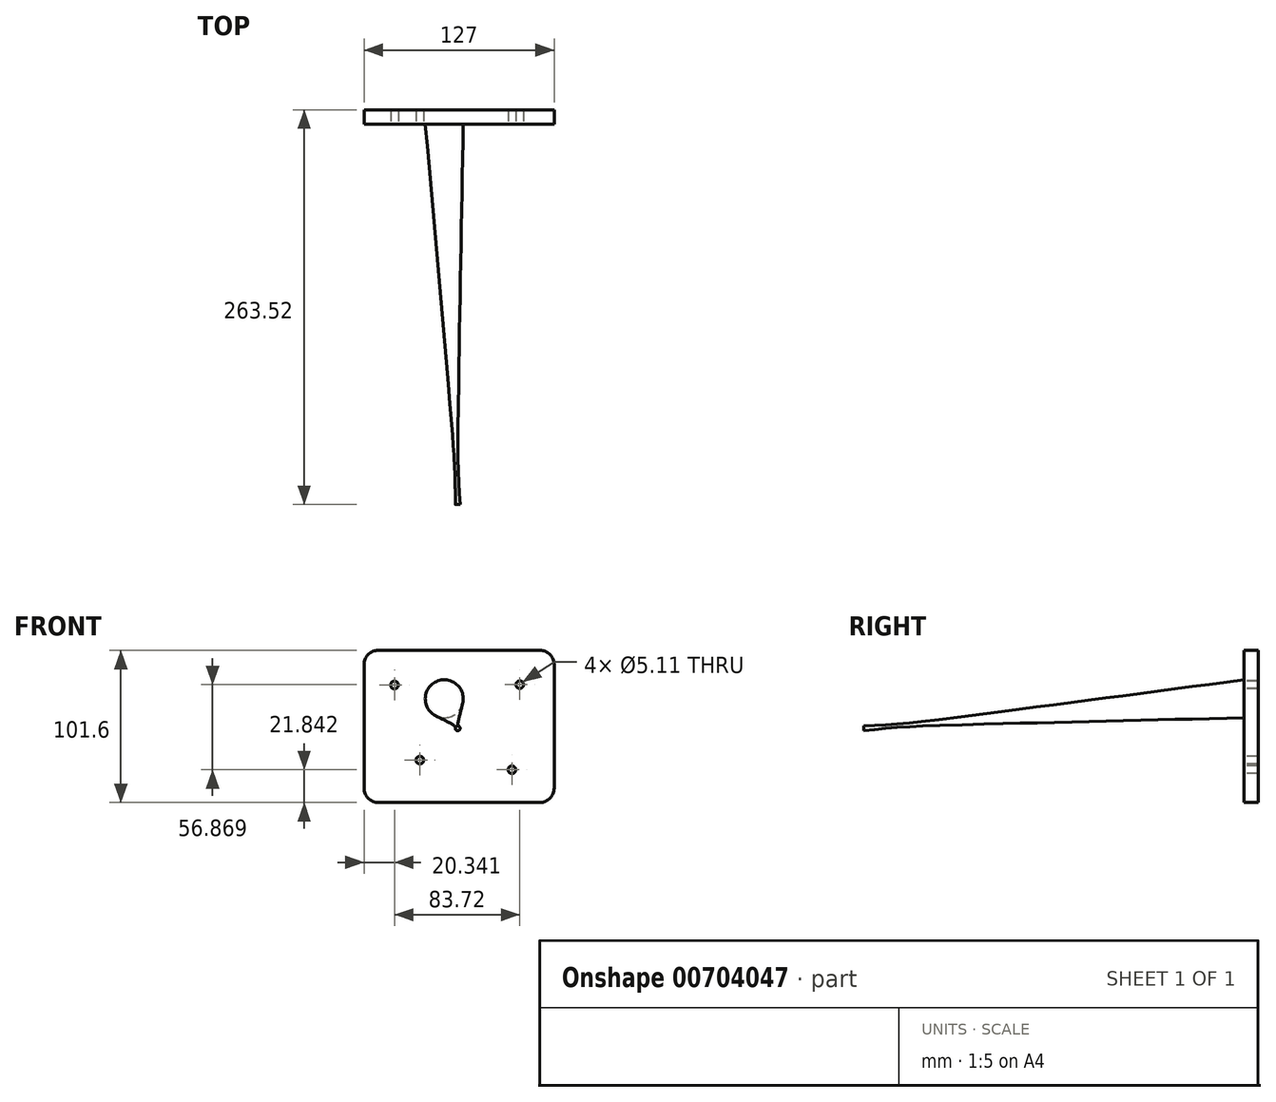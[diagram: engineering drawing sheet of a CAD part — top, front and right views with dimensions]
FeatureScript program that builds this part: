
annotation { "Feature Type Name" : "Feature", "Feature Type Description" : "" }
export const myFeature = defineFeature(function(context is Context, id is Id, definition is map)
    precondition{}
    {
        {
            var Q0;
            Q0=qCreatedBy(makeId("Front.planeOp"),FACE);
            var sketch = newSketch(context, id + "F0", { "sketchPlane" : qUnion([Q0])});
            skLineSegment(sketch, "E0.bottom", {"start": v(63.5, 50.8) * mm, "end": v(-63.5, 50.8) * mm});
            skLineSegment(sketch, "E0.top", {"start": v(63.5, -50.8) * mm, "end": v(-63.5, -50.8) * mm});
            skLineSegment(sketch, "E0.left", {"start": v(63.5, 50.8) * mm, "end": v(63.5, -50.8) * mm});
            skLineSegment(sketch, "E0.right", {"start": v(-63.5, 50.8) * mm, "end": v(-63.5, -50.8) * mm});
            skPoint(sketch, "E0.middle", {"position": v(0, 0) * mm});
            skSolve(sketch);
        }
        {
            var Q0;
            Q0=makeQuery(id+"F0.imprint","IMPRINT",FACE,{"disambiguationData":[TD([[makeQuery(id+"F0.imprint","IMPRINT",EDGE,{"derivedFrom":sQuery(id+"F0.wireOp",EDGE,"E0.bottom")}),1.0]])]});
            extrude(context, id + "F1", {"entities" : qUnion([Q0]), "endBound" : BoundingType.SYMMETRIC, "depth" : 9.52 * mm, "offsetDistance" : 25.4 * mm});
        }
        {
            var Q0;
            Q0=makeQuery(id+"F1.opExtrude","CAP_FACE",FACE,{"disambiguationData":[OSD([sQuery(id+"F0.wireOp",EDGE,"E0.bottom"),sQuery(id+"F0.wireOp",EDGE,"E0.top"),sQuery(id+"F0.wireOp",EDGE,"E0.left"),sQuery(id+"F0.wireOp",EDGE,"E0.right")])],"isStart":false});
            var sketch = newSketch(context, id + "F2", { "sketchPlane" : qUnion([Q0])});
            skPoint(sketch, "E1", {"position": v(-43.16, 27.68) * mm});
            skPoint(sketch, "E2", {"position": v(40.56, 27.91) * mm});
            skPoint(sketch, "E3", {"position": v(35.32, -28.96) * mm});
            skPoint(sketch, "E4", {"position": v(-26.2, -22.5) * mm});
            skSolve(sketch);
        }
        {
            var Q0;
            Q0=sQuery(id+"F2.wireOp",VERTEX,"E1");
            var Q1;
            Q1=sQuery(id+"F2.wireOp",VERTEX,"E4");
            var Q2;
            Q2=sQuery(id+"F2.wireOp",VERTEX,"E3");
            var Q3;
            Q3=sQuery(id+"F2.wireOp",VERTEX,"E2");
            var Q4;
            Q4=makeQuery(id+"F1.opExtrude","SWEPT_BODY",BODY,{"disambiguationData":[OSD([sQuery(id+"F0.wireOp",EDGE,"E0.bottom"),sQuery(id+"F0.wireOp",EDGE,"E0.top"),sQuery(id+"F0.wireOp",EDGE,"E0.left"),sQuery(id+"F0.wireOp",EDGE,"E0.right")])]});
            hole(context, id + "F3", {"style" : HoleStyle.SIMPLE, "endStyle" : HoleEndStyle.THROUGH, "standardTappedOrClearance" : lookupTablePath({ "standard" : "ANSI", "fit" : "Normal (ASME)", "engagement" : "75%", "pitch" : "20 tpi", "size" : "1/4", "type" : "Tapped" }), "standardBlindInLast" : lookupTablePath({ "fit" : "Free", "standard" : "ANSI", "engagement" : "75%", "pitch" : "20 tpi", "size" : "1/4", "type" : "Tapped" }), "holeDiameter" : 5.1 * mm, "majorDiameter" : 6.35 * mm, "showTappedDepth" : true, "isTappedThrough" : true, "tappedDepth" : 12.7 * mm, "tapClearance" : 3, "locations" : qUnion([Q0, Q1, Q2, Q3]), "scope" : qUnion([Q4])});
        }
        {
            var Q0;
            Q0=makeQuery(id+"F1.opExtrude","SWEPT_EDGE",EDGE,{"disambiguationData":[OSD([sQuery(id+"F0.wireOp",EDGE,"E0.bottom"),sQuery(id+"F0.wireOp",EDGE,"E0.left")])]});
            var Q1;
            Q1=makeQuery(id+"F1.opExtrude","SWEPT_EDGE",EDGE,{"disambiguationData":[OSD([sQuery(id+"F0.wireOp",EDGE,"E0.top"),sQuery(id+"F0.wireOp",EDGE,"E0.left")])]});
            var Q2;
            Q2=makeQuery(id+"F1.opExtrude","SWEPT_EDGE",EDGE,{"disambiguationData":[OSD([sQuery(id+"F0.wireOp",EDGE,"E0.bottom"),sQuery(id+"F0.wireOp",EDGE,"E0.right")])]});
            var Q3;
            Q3=makeQuery(id+"F1.opExtrude","SWEPT_EDGE",EDGE,{"disambiguationData":[OSD([sQuery(id+"F0.wireOp",EDGE,"E0.top"),sQuery(id+"F0.wireOp",EDGE,"E0.right")])]});
            fillet(context, id + "F4", {"entities" : qUnion([Q0, Q1, Q2, Q3]), "radius" : 9.52 * mm, "tangentPropagation" : true, "allowEdgeOverflow" : false});
        }
        {
            var Q0;
            Q0=makeQuery(id+"F1.opExtrude","CAP_FACE",FACE,{"disambiguationData":[OSD([sQuery(id+"F0.wireOp",EDGE,"E0.bottom"),sQuery(id+"F0.wireOp",EDGE,"E0.top"),sQuery(id+"F0.wireOp",EDGE,"E0.left"),sQuery(id+"F0.wireOp",EDGE,"E0.right")])],"isStart":false});
            var sketch = newSketch(context, id + "F5", { "sketchPlane" : qUnion([Q0])});
            skCircle(sketch, "E5", {"center": v(-9.88, 18.46) * mm, "radius": 12.7 * mm});
            skSolve(sketch);
        }
        {
            var Q0;
            Q0=makeQuery(id+"F5.imprint","IMPRINT",FACE,{"disambiguationData":[TD([[makeQuery(id+"F5.imprint","IMPRINT",EDGE,{"derivedFrom":sQuery(id+"F5.wireOp",EDGE,"E5")}),-1.0]])]});
            cPlane(context, id + "F6", {"entities" : qUnion([Q0]), "cplaneType" : CPlaneType.OFFSET, "offset" : 254 * mm, "width" : 152.4 * mm, "height" : 152.4 * mm});
        }
        {
            var Q0;
            Q0=qCreatedBy(id+"F6.planeOp",FACE);
            var sketch = newSketch(context, id + "F7", { "sketchPlane" : qUnion([Q0])});
            skCircle(sketch, "E6", {"center": v(-0.93, -1.29) * mm, "radius": 1.59 * mm});
            skSolve(sketch);
        }
        {
            var Q1;
            Q1 = qSketchRegion(id + "F5", true);
            var Q2;
            Q2 = qSketchRegion(id + "F7", true);
            loft(context, id + "F8", {"operationType" : NewBodyOperationType.ADD, "sheetProfilesArray" : [{ "sheetProfileEntities" : qUnion([Q1]) }, { "sheetProfileEntities" : qUnion([Q2]) }]});
        }
    });
